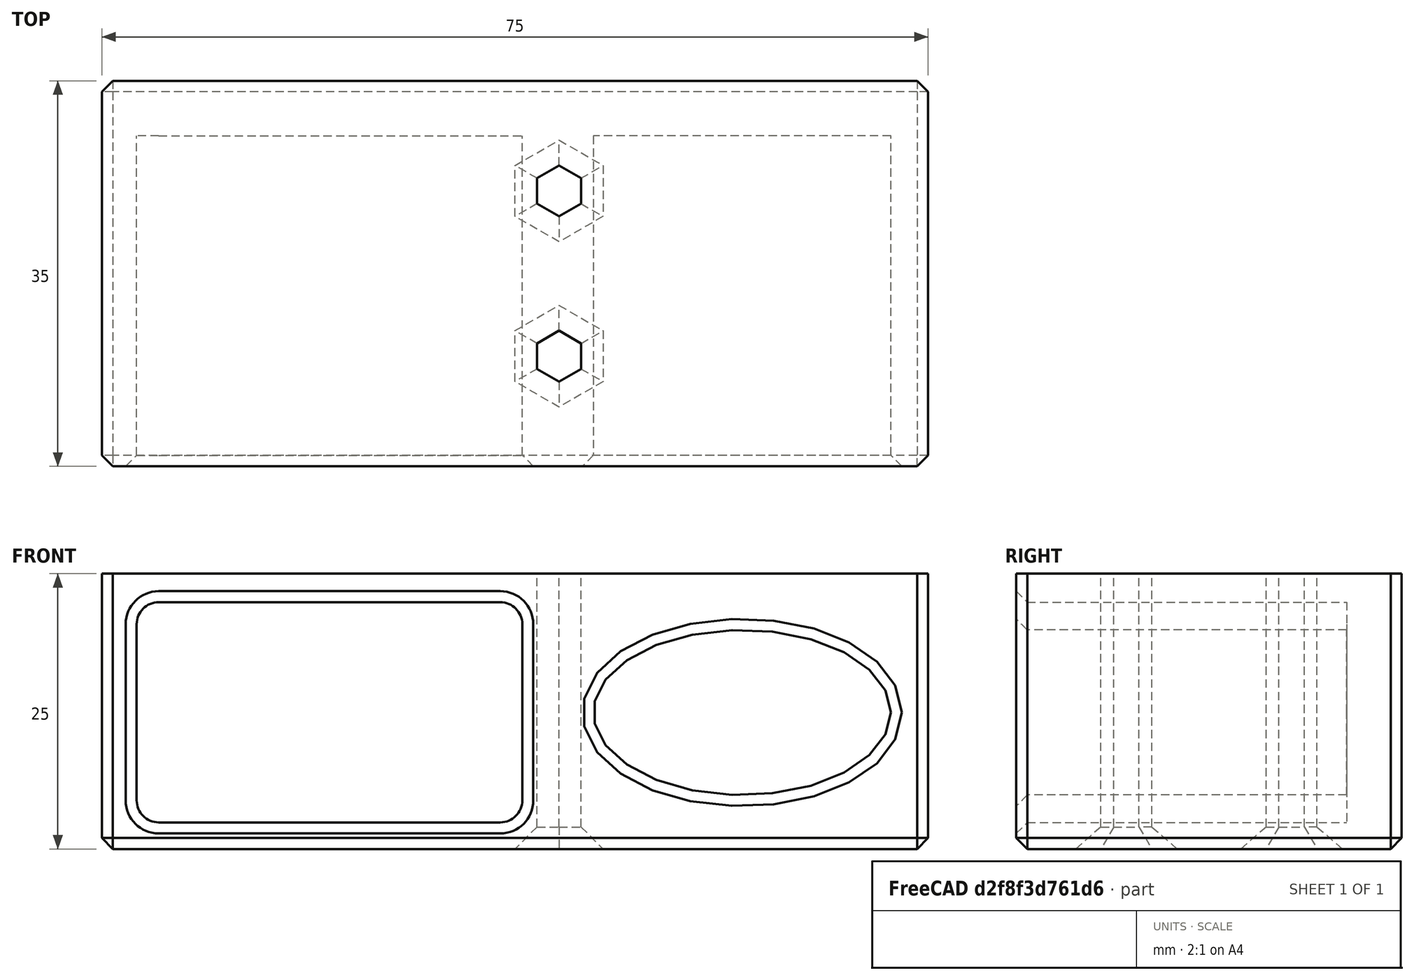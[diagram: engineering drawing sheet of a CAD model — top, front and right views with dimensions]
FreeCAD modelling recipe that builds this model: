
FCSTD DOCUMENT  (FreeCAD 0.19R)
Label: Flasholder
License: All rights reserved
LicenseURL: http://en.wikipedia.org/wiki/All_rights_reserved
objects: PartDesign::Chamfer×4, Sketcher::SketchObject×3, PartDesign::Pocket×2, PartDesign::Pad×1, PartDesign::Fillet×1, PartDesign::Body×1, Mesh::Feature×1
note: 20 computed .brp shape members not serialized (recipe doc carries the construction recipe); baked Part::Feature solids carry a one-line shape summary decoded from their .brp

FEATURE [Sketcher::SketchObject] Sketch
  FullyConstrained = true
  MapMode = 5
  Placement = pos=(0,0,0) rot=(1,0,0;1.5708rad)
  Support = -> [XZ_Plane]
  sketch-geometry (4):
    g0: LineSegment StartX=-37.5 StartY=12.5 StartZ=0 EndX=37.5 EndY=12.5 EndZ=0
    g1: LineSegment StartX=37.5 StartY=12.5 StartZ=0 EndX=37.5 EndY=-12.5 EndZ=0
    g2: LineSegment StartX=37.5 StartY=-12.5 StartZ=0 EndX=-37.5 EndY=-12.5 EndZ=0
    g3: LineSegment StartX=-37.5 StartY=-12.5 StartZ=0 EndX=-37.5 EndY=12.5 EndZ=0
  constraints (11):
    c: Coincident(g0,g1)
    c: Coincident(g1,g2)
    c: Coincident(g2,g3)
    c: Coincident(g3,g0)
    c: Horizontal(g0)
    c: Horizontal(g2)
    c: Vertical(g1)
    c: Vertical(g3)
    c: Distance(g0) = 75
    c: Distance(g1) = 25
    c: Symmetric(g1,g0,g-1)
FEATURE [PartDesign::Pad] Pad
  Direction = (1,1,1)
  Length = 35
  Length2 = 100
  Placement = pos=(0,0,0) rot=(1,0,0;1.5708rad)
  Profile = -> Sketch
  Type = 0
FEATURE [Sketcher::SketchObject] Sketch001
  FullyConstrained = false
  MapMode = 5
  Placement = pos=(0,-35,2.33e-14) rot=(1,0,0;1.5708rad)
  Support = -> [Pad]
  sketch-geometry (9):
    g0: LineSegment StartX=-34.3385 StartY=9.90893 StartZ=0 EndX=0.661503 EndY=9.90893 EndZ=0
    g1: LineSegment StartX=0.661503 StartY=9.90893 StartZ=0 EndX=0.661503 EndY=-10.0911 EndZ=0
    g2: LineSegment StartX=0.661503 StartY=-10.0911 StartZ=0 EndX=-34.3385 EndY=-10.0911 EndZ=0
    g3: LineSegment StartX=-34.3385 StartY=-10.0911 StartZ=0 EndX=-34.3385 EndY=9.90893 EndZ=0
    g4: Ellipse CenterX=20.6207 CenterY=-0.106726 CenterZ=0 NormalX=0 NormalY=0 NormalZ=1 MajorRadius=13.5 MinorRadius=7.5 AngleXU=0
    g5: LineSegment StartX=34.1207 StartY=-0.106726 StartZ=0 EndX=7.12072 EndY=-0.106726 EndZ=0
    g6: LineSegment StartX=20.6207 StartY=7.39327 StartZ=0 EndX=20.6207 EndY=-7.60673 EndZ=0
    g7: GeomPoint X=31.8457 Y=-0.106726 Z=0
    g8: GeomPoint X=9.39575 Y=-0.106726 Z=0
  constraints (14):
    c: Coincident(g0,g1)
    c: Coincident(g1,g2)
    c: Coincident(g2,g3)
    c: Coincident(g3,g0)
    c: Horizontal(g0)
    c: Horizontal(g2)
    c: Vertical(g1)
    c: Vertical(g3)
    c: Distance(g0) = 35
    c: Distance(g1) = 20
    c: InternalAlignment(g5-g8 -> g4) x4
    c: Distance(g6) = 15
    c: Distance(g5) = 27
    c: Horizontal(g5)
FEATURE [PartDesign::Pocket] Pocket
  BaseFeature = -> Pad
  Length = 30
  Length2 = 100
  Placement = pos=(0,0,0) rot=(1,0,0;1.5708rad)
  Profile = -> Sketch001
  Type = 0
FEATURE [Sketcher::SketchObject] Sketch002
  FullyConstrained = true
  MapMode = 5
  Placement = pos=(0,-1.39e-14,-12.5) rot=(1,0,0;3.14159rad)
  Support = -> [Pocket]
  sketch-geometry (14):
    g0: LineSegment StartX=4 StartY=22.6906 StartZ=0 EndX=6 EndY=23.8453 EndZ=0
    g1: LineSegment StartX=6 StartY=23.8453 StartZ=0 EndX=6 EndY=26.1547 EndZ=0
    g2: LineSegment StartX=6 StartY=26.1547 StartZ=0 EndX=4 EndY=27.3094 EndZ=0
    g3: LineSegment StartX=4 StartY=27.3094 StartZ=0 EndX=2 EndY=26.1547 EndZ=0
    g4: LineSegment StartX=2 StartY=26.1547 StartZ=0 EndX=2 EndY=23.8453 EndZ=0
    g5: LineSegment StartX=2 StartY=23.8453 StartZ=0 EndX=4 EndY=22.6906 EndZ=0
    g6: Circle CenterX=4 CenterY=25 CenterZ=0 NormalX=0 NormalY=0 NormalZ=1 AngleXU=0 Radius=2.3094
    g7: LineSegment StartX=4 StartY=7.6906 StartZ=0 EndX=6 EndY=8.8453 EndZ=0
    g8: LineSegment StartX=6 StartY=8.8453 StartZ=0 EndX=6 EndY=11.1547 EndZ=0
    g9: LineSegment StartX=6 StartY=11.1547 StartZ=0 EndX=4 EndY=12.3094 EndZ=0
    g10: LineSegment StartX=4 StartY=12.3094 StartZ=0 EndX=2 EndY=11.1547 EndZ=0
    g11: LineSegment StartX=2 StartY=11.1547 StartZ=0 EndX=2 EndY=8.8453 EndZ=0
    g12: LineSegment StartX=2 StartY=8.8453 StartZ=0 EndX=4 EndY=7.6906 EndZ=0
    g13: Circle CenterX=4 CenterY=10 CenterZ=0 NormalX=0 NormalY=0 NormalZ=1 AngleXU=0 Radius=2.3094
  constraints (34):
    c: Coincident(g0,g1)
    c: Coincident(g1,g2)
    c: Coincident(g2,g3)
    c: Coincident(g3,g4)
    c: Coincident(g4,g5)
    c: Coincident(g5,g0)
    c: Equal(g0, g1-g5) x5
    c: PointOnObject(g0,g6)
    c: PointOnObject(g1,g6)
    c: PointOnObject(g2,g6)
    c: PointOnObject(g3,g6)
    c: PointOnObject(g4,g6)
    c: PointOnObject(g5,g6)
    c: Coincident(g7,g8)
    c: Coincident(g8,g9)
    c: Coincident(g9,g10)
    c: Coincident(g10,g11)
    c: Coincident(g11,g12)
    c: Coincident(g12,g7)
    c: Equal(g7, g8-g12) x5
    c: PointOnObject(g7,g13)
    c: PointOnObject(g8,g13)
    c: PointOnObject(g9,g13)
    c: PointOnObject(g10,g13)
    c: PointOnObject(g11,g13)
    c: PointOnObject(g12,g13)
    c: Vertical(g1)
    c: Vertical(g8)
    c: Distance(g8,g10) = 4
    c: Distance(g1,g3) = 4
    c: DistanceX(g6) = 4
    c: DistanceX(g13) = 4
    c: DistanceY(g13) = 10
    c: DistanceY(g6) = 25
FEATURE [PartDesign::Pocket] Pocket001
  BaseFeature = -> Pocket
  Length = 5
  Length2 = 100
  Placement = pos=(0,0,0) rot=(1,0,0;1.5708rad)
  Profile = -> Sketch002
  Type = 1
FEATURE [PartDesign::Chamfer] Chamfer
  Angle = 45
  Base = -> Pocket001 [Edge42,Edge45,Edge47,Edge49,Edge51,Edge53,Edge30,Edge33,Edge35,Edge37,Edge39,Edge41]
  BaseFeature = -> Pocket001
  ChamferType = 0
  FlipDirection = false
  Placement = pos=(0,0,0) rot=(1,0,0;1.5708rad)
  Size = 2
  Size2 = 1
  SupportTransform = false
FEATURE [PartDesign::Chamfer] Chamfer001
  Angle = 45
  Base = -> Chamfer [Edge47,Edge41,Edge42,Edge49,Edge39,Edge48,Edge40,Edge46]
  BaseFeature = -> Chamfer
  ChamferType = 0
  FlipDirection = false
  Placement = pos=(0,0,0) rot=(1,0,0;1.5708rad)
  Size = 1
  Size2 = 1
  SupportTransform = false
FEATURE [PartDesign::Fillet] Fillet
  Base = -> Chamfer001 [Edge76,Edge75,Edge80,Edge78]
  BaseFeature = -> Chamfer001
  Placement = pos=(0,0,0) rot=(1,0,0;1.5708rad)
  Radius = 2
  SupportTransform = false
FEATURE [PartDesign::Chamfer] Chamfer002
  Angle = 45
  Base = -> Fillet [Edge5]
  BaseFeature = -> Fillet
  ChamferType = 0
  FlipDirection = false
  Placement = pos=(0,0,0) rot=(1,0,0;1.5708rad)
  Size = 1
  Size2 = 1
  SupportTransform = false
FEATURE [PartDesign::Chamfer] Chamfer003
  Angle = 45
  Base = -> Chamfer002 [Edge13]
  BaseFeature = -> Chamfer002
  ChamferType = 0
  FlipDirection = false
  Placement = pos=(0,0,0) rot=(1,0,0;1.5708rad)
  Size = 1
  Size2 = 1
  SupportTransform = false
FEATURE [PartDesign::Body] Body
  Group = -> [Sketch,Pad,Sketch001,Pocket,Sketch002,Pocket001,Chamfer,Chamfer001,Fillet,Chamfer002,Chamfer003]
  Origin = -> Origin
  Tip = -> Chamfer003
FEATURE [Mesh::Feature] Mesh  label="Chamfer003 (Meshed)"
